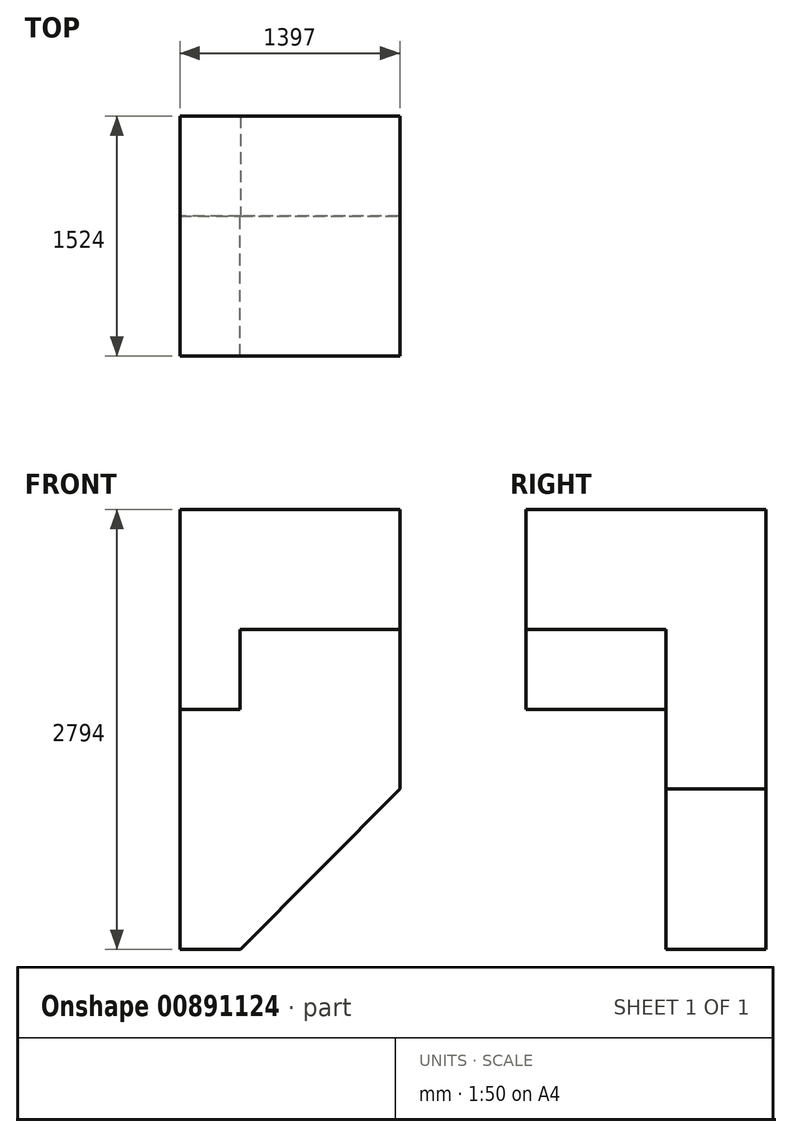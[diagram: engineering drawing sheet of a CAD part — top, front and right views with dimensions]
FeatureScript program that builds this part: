
annotation { "Feature Type Name" : "Feature", "Feature Type Description" : "" }
export const myFeature = defineFeature(function(context is Context, id is Id, definition is map)
    precondition{}
    {
        {
            var Q0;
            Q0=qCreatedBy(makeId("Front.planeOp"),FACE);
            var sketch = newSketch(context, id + "F0", { "sketchPlane" : qUnion([Q0])});
            skLineSegment(sketch, "E0.bottom", {"start": v(0, 0) * mm, "end": v(-1397, 0) * mm});
            skLineSegment(sketch, "E0.top", {"start": v(0, 2794) * mm, "end": v(-1397, 2794) * mm});
            skLineSegment(sketch, "E0.left", {"start": v(0, 0) * mm, "end": v(0, 2794) * mm});
            skLineSegment(sketch, "E0.right", {"start": v(-1397, 0) * mm, "end": v(-1397, 2794) * mm});
            skSolve(sketch);
        }
        {
            var Q0;
            Q0 = qSketchRegion(id + "F0", true);
            extrude(context, id + "F1", {"entities" : qUnion([Q0]), "depth" : 635 * mm, "offsetDistance" : 25.4 * mm});
        }
        {
            var Q0;
            Q0=makeQuery(id+"F1.opExtrude","CAP_FACE",FACE,{"disambiguationData":[OSD([sQuery(id+"F0.wireOp",EDGE,"E0.bottom"),sQuery(id+"F0.wireOp",EDGE,"E0.top"),sQuery(id+"F0.wireOp",EDGE,"E0.left"),sQuery(id+"F0.wireOp",EDGE,"E0.right")])],"isStart":false});
            var sketch = newSketch(context, id + "F2", { "sketchPlane" : qUnion([Q0])});
            skLineSegment(sketch, "E1.bottom", {"start": v(0, 2794) * mm, "end": v(-1016, 2794) * mm});
            skLineSegment(sketch, "E1.top", {"start": v(0, 2032) * mm, "end": v(-1016, 2032) * mm});
            skLineSegment(sketch, "E1.left", {"start": v(0, 2794) * mm, "end": v(0, 2032) * mm});
            skLineSegment(sketch, "E1.right", {"start": v(-1016, 2794) * mm, "end": v(-1016, 2032) * mm});
            skSolve(sketch);
        }
        {
            var Q0;
            Q0 = qSketchRegion(id + "F2", true);
            extrude(context, id + "F3", {"entities" : qUnion([Q0]), "operationType" : NewBodyOperationType.ADD, "depth" : 889 * mm, "offsetDistance" : 25.4 * mm});
        }
        {
            var Q0;
            Q0=makeQuery(id+"F1.opExtrude","CAP_FACE",FACE,{"disambiguationData":[OSD([sQuery(id+"F0.wireOp",EDGE,"E0.bottom"),sQuery(id+"F0.wireOp",EDGE,"E0.top"),sQuery(id+"F0.wireOp",EDGE,"E0.left"),sQuery(id+"F0.wireOp",EDGE,"E0.right")])],"isStart":false});
            var sketch = newSketch(context, id + "F4", { "sketchPlane" : qUnion([Q0])});
            skLineSegment(sketch, "E2.bottom", {"start": v(-1397, 2794) * mm, "end": v(-1016, 2794) * mm});
            skLineSegment(sketch, "E2.top", {"start": v(-1397, 1524) * mm, "end": v(-1016, 1524) * mm});
            skLineSegment(sketch, "E2.left", {"start": v(-1397, 2794) * mm, "end": v(-1397, 1524) * mm});
            skLineSegment(sketch, "E2.right", {"start": v(-1016, 2794) * mm, "end": v(-1016, 1524) * mm});
            skSolve(sketch);
        }
        {
            var Q0;
            Q0 = qSketchRegion(id + "F4", true);
            extrude(context, id + "F5", {"entities" : qUnion([Q0]), "operationType" : NewBodyOperationType.ADD, "depth" : 889 * mm, "offsetDistance" : 25.4 * mm});
        }
        {
            var Q0;
            Q0=makeQuery(id+"F1.opExtrude","CAP_FACE",FACE,{"disambiguationData":[OSD([sQuery(id+"F0.wireOp",EDGE,"E0.bottom"),sQuery(id+"F0.wireOp",EDGE,"E0.top"),sQuery(id+"F0.wireOp",EDGE,"E0.left"),sQuery(id+"F0.wireOp",EDGE,"E0.right")])],"isStart":false});
            var sketch = newSketch(context, id + "F6", { "sketchPlane" : qUnion([Q0])});
            skLineSegment(sketch, "E3.bottom", {"start": v(-1397, 0) * mm, "end": v(-1016, 0) * mm});
            skLineSegment(sketch, "E3.top", {"start": v(-1397, 635) * mm, "end": v(-1016, 635) * mm});
            skLineSegment(sketch, "E3.left", {"start": v(-1397, 0) * mm, "end": v(-1397, 635) * mm});
            skLineSegment(sketch, "E3.right", {"start": v(-1016, 0) * mm, "end": v(-1016, 635) * mm});
            skSolve(sketch);
        }
        {
            var Q0;
            {var subQ3=sQuery(id+"F6.wireOp",EDGE,"E3.top");Q0=makeQuery(id+"F6.imprint","IMPRINT",FACE,{"disambiguationData":[TD([[makeQuery(id+"F6.imprint","IMPRINT",EDGE,{"derivedFrom":subQ3}),1.0]])]});}
            var sketch = newSketch(context, id + "F7", { "sketchPlane" : qUnion([Q0])});
            skLineSegment(sketch, "E4", {"start": v(-1011.43, 0) * mm, "end": v(0, 1020.35) * mm});
            skSolve(sketch);
        }
        {
            var Q0;
            {var subQ0=sQuery(id+"F7.wireOp",EDGE,"E4");Q0=makeQuery(id+"F7.imprint","IMPRINT",FACE,{"disambiguationData":[TD([[makeQuery(id+"F7.imprint","IMPRINT",EDGE,{"derivedFrom":subQ0}),-1.0]])]});}
            extrude(context, id + "F8", {"entities" : qUnion([Q0]), "operationType" : NewBodyOperationType.REMOVE, "oppositeDirection" : true, "depth" : 949.96 * mm, "offsetDistance" : 25.4 * mm});
        }
    });
